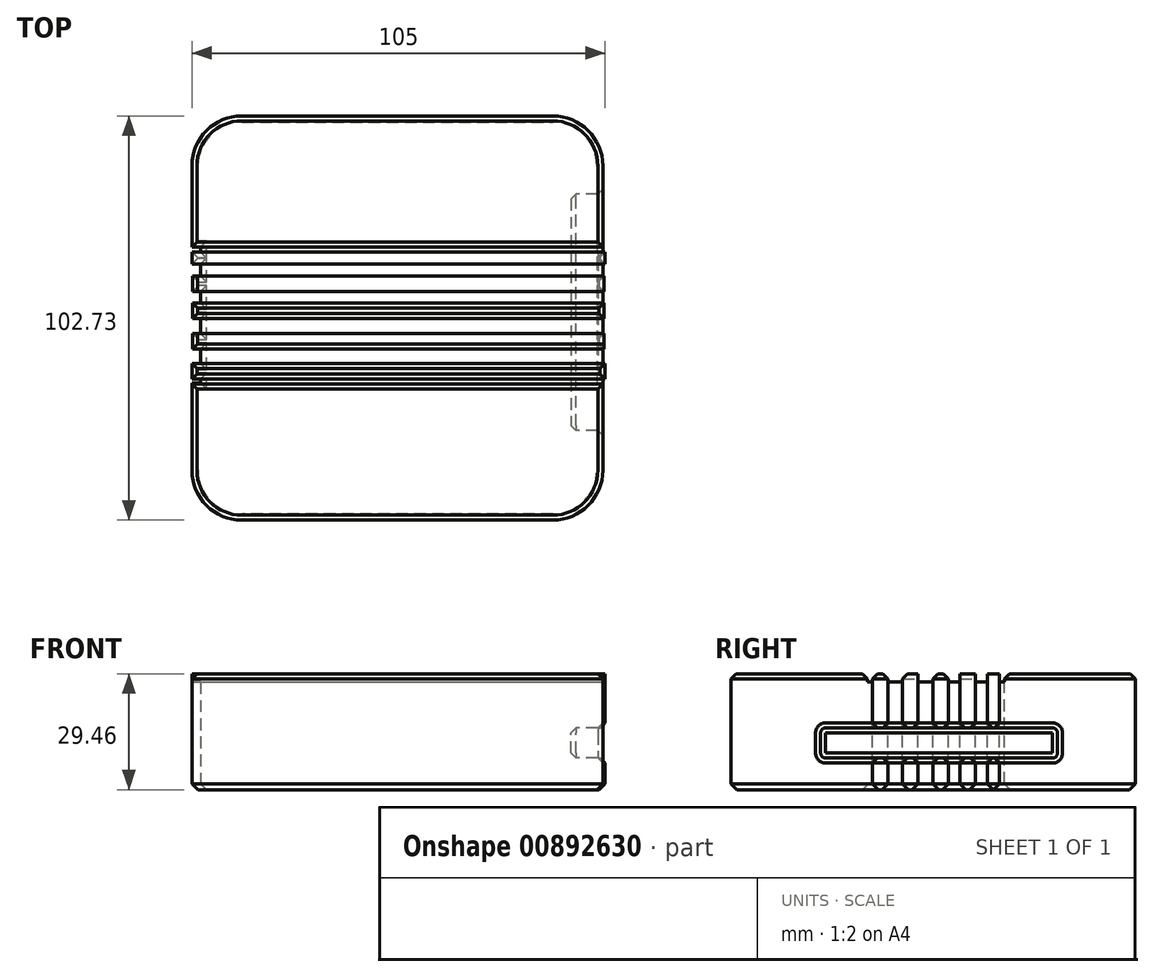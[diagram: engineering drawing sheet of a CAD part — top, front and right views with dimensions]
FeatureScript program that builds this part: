
annotation { "Feature Type Name" : "Feature", "Feature Type Description" : "" }
export const myFeature = defineFeature(function(context is Context, id is Id, definition is map)
    precondition{}
    {
        {
            var Q0;
            Q0=qCreatedBy(makeId("Top.planeOp"),FACE);
            var sketch = newSketch(context, id + "F0", { "sketchPlane" : qUnion([Q0])});
            skLineSegment(sketch, "E0.bottom", {"start": v(-52.2, 52.34) * mm, "end": v(52.2, 52.34) * mm});
            skLineSegment(sketch, "E0.top", {"start": v(-52.2, -50.4) * mm, "end": v(52.2, -50.4) * mm});
            skLineSegment(sketch, "E0.left", {"start": v(-52.2, 52.34) * mm, "end": v(-52.2, -50.4) * mm});
            skLineSegment(sketch, "E0.right", {"start": v(52.2, 52.34) * mm, "end": v(52.2, -50.4) * mm});
            skSolve(sketch);
        }
        {
            var Q0;
            Q0 = qSketchRegion(id + "F0", true);
            extrude(context, id + "F1", {"entities" : qUnion([Q0]), "depth" : 25.4 * mm, "offsetDistance" : 25.4 * mm});
        }
        {
            var Q0;
            Q0=makeQuery(id+"F1.opExtrude","SWEPT_EDGE",EDGE,{"disambiguationData":[OSD([sQuery(id+"F0.wireOp",EDGE,"E0.top"),sQuery(id+"F0.wireOp",EDGE,"E0.left")])]});
            var Q1;
            Q1=makeQuery(id+"F1.opExtrude","SWEPT_EDGE",EDGE,{"disambiguationData":[OSD([sQuery(id+"F0.wireOp",EDGE,"E0.top"),sQuery(id+"F0.wireOp",EDGE,"E0.right")])]});
            var Q2;
            Q2=makeQuery(id+"F1.opExtrude","SWEPT_EDGE",EDGE,{"disambiguationData":[OSD([sQuery(id+"F0.wireOp",EDGE,"E0.bottom"),sQuery(id+"F0.wireOp",EDGE,"E0.left")])]});
            var Q3;
            Q3=makeQuery(id+"F1.opExtrude","SWEPT_EDGE",EDGE,{"disambiguationData":[OSD([sQuery(id+"F0.wireOp",EDGE,"E0.bottom"),sQuery(id+"F0.wireOp",EDGE,"E0.right")])]});
            fillet(context, id + "F2", {"entities" : qUnion([Q0, Q1, Q2, Q3]), "radius" : 12.7 * mm, "tangentPropagation" : true, "allowEdgeOverflow" : false});
        }
        {
            var Q0;
            Q0=makeQuery(id+"F1.opExtrude","CAP_FACE",FACE,{"disambiguationData":[OSD([sQuery(id+"F0.wireOp",EDGE,"E0.bottom"),sQuery(id+"F0.wireOp",EDGE,"E0.top"),sQuery(id+"F0.wireOp",EDGE,"E0.left"),sQuery(id+"F0.wireOp",EDGE,"E0.right")])],"isStart":false});
            var sketch = newSketch(context, id + "F3", { "sketchPlane" : qUnion([Q0])});
            skLineSegment(sketch, "E1.bottom", {"start": v(-52.2, 19.05) * mm, "end": v(52.2, 19.05) * mm});
            skLineSegment(sketch, "E1.top", {"start": v(-52.2, -15.75) * mm, "end": v(52.2, -15.75) * mm});
            skLineSegment(sketch, "E1.left", {"start": v(-52.2, 19.05) * mm, "end": v(-52.2, -15.75) * mm});
            skLineSegment(sketch, "E1.right", {"start": v(52.2, 19.05) * mm, "end": v(52.2, -15.75) * mm});
            skSolve(sketch);
        }
        {
            var Q0;
            Q0=makeQuery(id+"F3.imprint","IMPRINT",FACE,{"disambiguationData":[TD([[makeQuery(id+"F3.imprint","IMPRINT",EDGE,{"derivedFrom":sQuery(id+"F3.wireOp",EDGE,"E1.bottom")}),-1.0]])]});
            extrude(context, id + "F4", {"entities" : qUnion([Q0]), "operationType" : NewBodyOperationType.REMOVE, "oppositeDirection" : true, "depth" : 2.15 * mm, "offsetDistance" : 25.4 * mm});
        }
        {
            var Q0;
            Q0=makeQuery(id+"F1.opExtrude","SWEPT_FACE",FACE,{"disambiguationData":[OSD([sQuery(id+"F0.wireOp",EDGE,"E0.left")])]});
            var sketch = newSketch(context, id + "F5", { "sketchPlane" : qUnion([Q0])});
            skLineSegment(sketch, "E2.bottom", {"start": v(-19.05, 23.25) * mm, "end": v(15.58, 23.25) * mm});
            skLineSegment(sketch, "E2.top", {"start": v(-19.05, 0) * mm, "end": v(15.58, 0) * mm});
            skLineSegment(sketch, "E2.left", {"start": v(-19.05, 23.25) * mm, "end": v(-19.05, 0) * mm});
            skLineSegment(sketch, "E2.right", {"start": v(15.58, 23.25) * mm, "end": v(15.58, 0) * mm});
            skSolve(sketch);
        }
        {
            var Q0;
            Q0=makeQuery(id+"F5.imprint","IMPRINT",FACE,{"disambiguationData":[TD([[makeQuery(id+"F5.imprint","IMPRINT",EDGE,{"derivedFrom":sQuery(id+"F5.wireOp",EDGE,"E2.bottom")}),-1.0]])]});
            extrude(context, id + "F6", {"entities" : qUnion([Q0]), "operationType" : NewBodyOperationType.REMOVE, "oppositeDirection" : true, "depth" : 2.27 * mm, "offsetDistance" : 25.4 * mm});
        }
        {
            var Q0;
            {var subQ0=sQuery(id+"F0.wireOp",EDGE,"E0.left");var subQ1=sQuery(id+"F0.wireOp",EDGE,"E0.bottom");var subQ2=sQuery(id+"F0.wireOp",EDGE,"E0.right");Q0=makeQuery(id+"F4.boolean.opBoolean","SPLIT",FACE,{"disambiguationData":[TD([makeQuery(id+"F1.opExtrude","SWEPT_FACE",FACE,{"disambiguationData":[OSD([subQ1])]})])],"derivedFrom":makeQuery(id+"F1.opExtrude","CAP_FACE",FACE,{"disambiguationData":[OSD([subQ1,sQuery(id+"F0.wireOp",EDGE,"E0.top"),subQ0,subQ2])],"isStart":false})});}
            var sketch = newSketch(context, id + "F7", { "sketchPlane" : qUnion([Q0])});
            skLineSegment(sketch, "E3.bottom", {"start": v(-52.06, 11.67) * mm, "end": v(52.53, 11.67) * mm});
            skLineSegment(sketch, "E3.top", {"start": v(-52.06, 7.72) * mm, "end": v(52.53, 7.72) * mm});
            skLineSegment(sketch, "E3.left", {"start": v(-52.06, 11.67) * mm, "end": v(-52.06, 7.72) * mm});
            skLineSegment(sketch, "E3.right", {"start": v(52.53, 11.67) * mm, "end": v(52.53, 7.72) * mm});
            skLineSegment(sketch, "E4.bottom", {"start": v(-52.03, 4.82) * mm, "end": v(52.56, 4.82) * mm});
            skLineSegment(sketch, "E4.top", {"start": v(-52.03, 0.87) * mm, "end": v(52.56, 0.87) * mm});
            skLineSegment(sketch, "E4.left", {"start": v(-52.03, 4.82) * mm, "end": v(-52.03, 0.87) * mm});
            skLineSegment(sketch, "E4.right", {"start": v(52.56, 4.82) * mm, "end": v(52.56, 0.87) * mm});
            skLineSegment(sketch, "E5.bottom", {"start": v(-52.03, -2.9) * mm, "end": v(52.56, -2.9) * mm});
            skLineSegment(sketch, "E5.top", {"start": v(-52.03, -6.85) * mm, "end": v(52.56, -6.85) * mm});
            skLineSegment(sketch, "E5.left", {"start": v(-52.03, -2.9) * mm, "end": v(-52.03, -6.85) * mm});
            skLineSegment(sketch, "E5.right", {"start": v(52.56, -2.9) * mm, "end": v(52.56, -6.85) * mm});
            skLineSegment(sketch, "E6.bottom", {"start": v(-52.2, -10.52) * mm, "end": v(52.81, -10.52) * mm});
            skLineSegment(sketch, "E6.top", {"start": v(-52.2, -14.47) * mm, "end": v(52.81, -14.47) * mm});
            skLineSegment(sketch, "E6.left", {"start": v(-52.2, -10.52) * mm, "end": v(-52.2, -14.47) * mm});
            skLineSegment(sketch, "E6.right", {"start": v(52.81, -10.52) * mm, "end": v(52.81, -14.47) * mm});
            skLineSegment(sketch, "E7.bottom", {"start": v(-52.2, 14.7) * mm, "end": v(52.77, 14.7) * mm});
            skLineSegment(sketch, "E7.top", {"start": v(-52.2, 17.76) * mm, "end": v(52.77, 17.76) * mm});
            skLineSegment(sketch, "E7.left", {"start": v(-52.2, 14.7) * mm, "end": v(-52.2, 17.76) * mm});
            skLineSegment(sketch, "E7.right", {"start": v(52.77, 14.7) * mm, "end": v(52.77, 17.76) * mm});
            skSolve(sketch);
        }
        {
            var Q0;
            Q0=makeQuery(id+"F7.imprint","IMPRINT",FACE,{"disambiguationData":[TD([[makeQuery(id+"F7.imprint","IMPRINT",EDGE,{"derivedFrom":sQuery(id+"F7.wireOp",EDGE,"E6.bottom")}),-1.0]])]});
            var Q1;
            Q1=makeQuery(id+"F7.imprint","IMPRINT",FACE,{"disambiguationData":[TD([[makeQuery(id+"F7.imprint","IMPRINT",EDGE,{"derivedFrom":sQuery(id+"F7.wireOp",EDGE,"E5.bottom")}),-1.0]])]});
            var Q2;
            Q2=makeQuery(id+"F7.imprint","IMPRINT",FACE,{"disambiguationData":[TD([[makeQuery(id+"F7.imprint","IMPRINT",EDGE,{"derivedFrom":sQuery(id+"F7.wireOp",EDGE,"E4.bottom")}),-1.0]])]});
            var Q3;
            Q3=makeQuery(id+"F7.imprint","IMPRINT",FACE,{"disambiguationData":[TD([[makeQuery(id+"F7.imprint","IMPRINT",EDGE,{"derivedFrom":sQuery(id+"F7.wireOp",EDGE,"E3.bottom")}),-1.0]])]});
            var Q4;
            Q4=makeQuery(id+"F7.imprint","IMPRINT",FACE,{"disambiguationData":[TD([[makeQuery(id+"F7.imprint","IMPRINT",EDGE,{"derivedFrom":sQuery(id+"F7.wireOp",EDGE,"ohG4q9yi-Sl1K-y0JQ-5TuS-v2TCGCpd6eug.top")}),1.0]])]});
            var Q5;
            Q5=makeQuery(id+"F7.imprint","IMPRINT",FACE,{"disambiguationData":[TD([[makeQuery(id+"F7.imprint","IMPRINT",EDGE,{"derivedFrom":sQuery(id+"F7.wireOp",EDGE,"E7.bottom")}),1.0]])]});
            extrude(context, id + "F8", {"entities" : qUnion([Q0, Q1, Q2, Q3, Q4, Q5]), "operationType" : NewBodyOperationType.ADD, "oppositeDirection" : true, "depth" : 25.4 * mm, "offsetDistance" : 25.4 * mm});
        }
        {
            var Q0;
            {var subQ0=sQuery(id+"F0.wireOp",EDGE,"E0.left");Q0=makeQuery(id+"F4.boolean.opBoolean","SPLIT",EDGE,{"disambiguationData":[TD([makeQuery(id+"F4.opExtrude","SWEPT_FACE",FACE,{"disambiguationData":[OSD([sQuery(id+"F3.wireOp",EDGE,"E1.bottom")])]})])],"derivedFrom":makeQuery(id+"F1.opExtrude","CAP_EDGE",EDGE,{"disambiguationData":[OSD([subQ0])],"isStart":false})});}
            var Q1;
            {var subQ0=sQuery(id+"F0.wireOp",EDGE,"E0.left");var subQ1=sQuery(id+"F0.wireOp",EDGE,"E0.bottom");Q1=makeQuery(id+"F2.opFillet","BLEND_EDGE",EDGE,{"blendedFrom":[makeQuery(id+"F1.opExtrude","SWEPT_EDGE",EDGE,{"disambiguationData":[OSD([subQ1,subQ0])]}),makeQuery(id+"F1.opExtrude","CAP_FACE",FACE,{"disambiguationData":[OSD([subQ1,sQuery(id+"F0.wireOp",EDGE,"E0.top"),subQ0,sQuery(id+"F0.wireOp",EDGE,"E0.right")])],"isStart":false})],"blendedInto":[makeQuery(id+"F1.opExtrude","CAP_FACE",FACE,{"disambiguationData":[OSD([subQ1,sQuery(id+"F0.wireOp",EDGE,"E0.top"),subQ0,sQuery(id+"F0.wireOp",EDGE,"E0.right")])],"isStart":false})]});}
            var Q2;
            {var subQ0=sQuery(id+"F0.wireOp",EDGE,"E0.left");var subQ1=sQuery(id+"F0.wireOp",EDGE,"E0.bottom");var subQ2=sQuery(id+"F0.wireOp",EDGE,"E0.right");Q2=makeQuery(id+"F4.boolean.opBoolean","SPLIT",FACE,{"disambiguationData":[TD([makeQuery(id+"F1.opExtrude","SWEPT_FACE",FACE,{"disambiguationData":[OSD([subQ1])]})])],"derivedFrom":makeQuery(id+"F1.opExtrude","CAP_FACE",FACE,{"disambiguationData":[OSD([subQ1,sQuery(id+"F0.wireOp",EDGE,"E0.top"),subQ0,subQ2])],"isStart":false})});}
            var Q3;
            Q3=makeQuery(id+"F8.opExtrude","CAP_FACE",FACE,{"disambiguationData":[OSD([sQuery(id+"F7.wireOp",EDGE,"E6.bottom"),sQuery(id+"F7.wireOp",EDGE,"E6.top"),sQuery(id+"F7.wireOp",EDGE,"E6.left"),sQuery(id+"F7.wireOp",EDGE,"E6.right")])],"isStart":true});
            var Q4;
            Q4=makeQuery(id+"F8.opExtrude","CAP_EDGE",EDGE,{"disambiguationData":[OSD([sQuery(id+"F7.wireOp",EDGE,"E5.top")])],"isStart":true});
            var Q5;
            Q5=makeQuery(id+"F8.opExtrude","CAP_FACE",FACE,{"disambiguationData":[OSD([sQuery(id+"F7.wireOp",EDGE,"E4.bottom"),sQuery(id+"F7.wireOp",EDGE,"E4.top"),sQuery(id+"F7.wireOp",EDGE,"E4.left"),sQuery(id+"F7.wireOp",EDGE,"E4.right")])],"isStart":true});
            var Q6;
            Q6=makeQuery(id+"F8.opExtrude","CAP_EDGE",EDGE,{"disambiguationData":[OSD([sQuery(id+"F7.wireOp",EDGE,"E3.left")])],"isStart":true});
            var Q7;
            Q7=makeQuery(id+"F8.opExtrude","CAP_EDGE",EDGE,{"disambiguationData":[OSD([sQuery(id+"F7.wireOp",EDGE,"E4.left")])],"isStart":true});
            var Q8;
            Q8=makeQuery(id+"F8.opExtrude","CAP_EDGE",EDGE,{"disambiguationData":[OSD([sQuery(id+"F7.wireOp",EDGE,"E5.left")])],"isStart":true});
            var Q9;
            {var subQ0=sQuery(id+"F0.wireOp",EDGE,"E0.right");var subQ1=sQuery(id+"F0.wireOp",EDGE,"E0.left");var subQ2=sQuery(id+"F0.wireOp",EDGE,"E0.top");Q9=makeQuery(id+"F4.boolean.opBoolean","SPLIT",FACE,{"disambiguationData":[TD([makeQuery(id+"F1.opExtrude","SWEPT_FACE",FACE,{"disambiguationData":[OSD([subQ2])]})])],"derivedFrom":makeQuery(id+"F1.opExtrude","CAP_FACE",FACE,{"disambiguationData":[OSD([sQuery(id+"F0.wireOp",EDGE,"E0.bottom"),subQ2,subQ1,subQ0])],"isStart":false})});}
            chamfer(context, id + "F9", {"entities" : qUnion([Q0, Q1, Q2, Q3, Q4, Q5, Q6, Q7, Q8, Q9]), "width" : 1.27 * mm, "tangentPropagation" : true});
        }
        {
            var Q0;
            {var subQ1=sQuery(id+"F3.wireOp",EDGE,"E1.top");var subQ2=sQuery(id+"F0.wireOp",EDGE,"E0.right");Q0=makeQuery(id+"F8.boolean.opBoolean","SPLIT",FACE,{"disambiguationData":[TD([makeQuery(id+"F4.boolean.opBoolean","COPY",FACE,{"derivedFrom":makeQuery(id+"F4.opExtrude","SWEPT_FACE",FACE,{"disambiguationData":[OSD([subQ1])]})})])],"derivedFrom":makeQuery(id+"F1.opExtrude","SWEPT_FACE",FACE,{"disambiguationData":[OSD([subQ2])]})});}
            var sketch = newSketch(context, id + "F10", { "sketchPlane" : qUnion([Q0])});
            skPoint(sketch, "E8.firstSnap0", {"position": v(-14.47, 11.62) * mm});
            skLineSegment(sketch, "E8.bottom", {"start": v(-26.38, 11.62) * mm, "end": v(31.25, 11.62) * mm});
            skLineSegment(sketch, "E8.top", {"start": v(-26.38, 3.94) * mm, "end": v(31.25, 3.94) * mm});
            skLineSegment(sketch, "E8.left", {"start": v(-27.65, 10.35) * mm, "end": v(-27.65, 5.21) * mm});
            skLineSegment(sketch, "E8.right", {"start": v(32.52, 10.35) * mm, "end": v(32.52, 5.21) * mm});
            skPoint(sketch, "E9.visualSharp", {"position": v(-27.65, 11.62) * mm});
            skArc(sketch, "E9.filletArc", {"start": v(-26.38, 11.62) * mm, "mid": v(-27.28, 11.25) * mm, "end": v(-27.65, 10.35) * mm});
            skPoint(sketch, "E10.visualSharp", {"position": v(-27.65, 3.94) * mm});
            skArc(sketch, "E10.filletArc", {"start": v(-27.65, 5.21) * mm, "mid": v(-27.28, 4.32) * mm, "end": v(-26.38, 3.94) * mm});
            skPoint(sketch, "E11.visualSharp", {"position": v(32.52, 3.94) * mm});
            skArc(sketch, "E11.filletArc", {"start": v(31.25, 3.94) * mm, "mid": v(32.15, 4.32) * mm, "end": v(32.52, 5.21) * mm});
            skPoint(sketch, "E12.visualSharp", {"position": v(32.52, 11.62) * mm});
            skArc(sketch, "E12.filletArc", {"start": v(32.52, 10.35) * mm, "mid": v(32.15, 11.25) * mm, "end": v(31.25, 11.62) * mm});
            skSolve(sketch);
        }
        {
            var Q0;
            Q0 = qSketchRegion(id + "F10", true);
            extrude(context, id + "F11", {"entities" : qUnion([Q0]), "operationType" : NewBodyOperationType.REMOVE, "depth" : 18.54 * mm, "offsetDistance" : 25.4 * mm, "hasSecondDirection" : true, "secondDirectionOppositeDirection" : true, "secondDirectionDepth" : 8.13 * mm});
        }
        {
            var Q0;
            {var subQ1=sQuery(id+"F3.wireOp",EDGE,"E1.top");var subQ2=sQuery(id+"F0.wireOp",EDGE,"E0.right");Q0=makeQuery(id+"F11.boolean.opBoolean","INTERSECT",EDGE,{"derivedFrom":[makeQuery(id+"F8.boolean.opBoolean","SPLIT",FACE,{"disambiguationData":[TD([makeQuery(id+"F4.boolean.opBoolean","COPY",FACE,{"derivedFrom":makeQuery(id+"F4.opExtrude","SWEPT_FACE",FACE,{"disambiguationData":[OSD([subQ1])]})})])],"derivedFrom":makeQuery(id+"F1.opExtrude","SWEPT_FACE",FACE,{"disambiguationData":[OSD([subQ2])]})}),makeQuery(id+"F11.opExtrude","SWEPT_FACE",FACE,{"disambiguationData":[OSD([sQuery(id+"F10.wireOp",EDGE,"E8.bottom")])]})]});}
            var Q1;
            {var subQ1=sQuery(id+"F3.wireOp",EDGE,"E1.bottom");var subQ2=sQuery(id+"F0.wireOp",EDGE,"E0.right");Q1=makeQuery(id+"F11.boolean.opBoolean","INTERSECT",EDGE,{"derivedFrom":[makeQuery(id+"F8.boolean.opBoolean","SPLIT",FACE,{"disambiguationData":[TD([makeQuery(id+"F4.boolean.opBoolean","COPY",FACE,{"derivedFrom":makeQuery(id+"F4.opExtrude","SWEPT_FACE",FACE,{"disambiguationData":[OSD([subQ1])]})})])],"derivedFrom":makeQuery(id+"F1.opExtrude","SWEPT_FACE",FACE,{"disambiguationData":[OSD([subQ2])]})}),makeQuery(id+"F11.opExtrude","SWEPT_FACE",FACE,{"disambiguationData":[OSD([sQuery(id+"F10.wireOp",EDGE,"E8.bottom")])]})]});}
            var Q2;
            Q2=makeQuery(id+"F11.boolean.opBoolean","INTERSECT",EDGE,{"derivedFrom":[makeQuery(id+"F8.opExtrude","SWEPT_FACE",FACE,{"disambiguationData":[OSD([sQuery(id+"F7.wireOp",EDGE,"E7.right")])]}),makeQuery(id+"F11.opExtrude","SWEPT_FACE",FACE,{"disambiguationData":[OSD([sQuery(id+"F10.wireOp",EDGE,"E8.top")])]})]});
            var Q3;
            Q3=makeQuery(id+"F11.boolean.opBoolean","COPY",FACE,{"derivedFrom":makeQuery(id+"F11.opExtrude","SWEPT_FACE",FACE,{"disambiguationData":[OSD([sQuery(id+"F10.wireOp",EDGE,"E8.top")])]})});
            var Q4;
            Q4=makeQuery(id+"F11.boolean.opBoolean","COPY",FACE,{"derivedFrom":makeQuery(id+"F11.opExtrude","SWEPT_FACE",FACE,{"disambiguationData":[OSD([sQuery(id+"F10.wireOp",EDGE,"E8.bottom")])]})});
            chamfer(context, id + "F12", {"entities" : qUnion([Q0, Q1, Q2, Q3, Q4]), "width" : 1.27 * mm, "tangentPropagation" : true});
        }
        {
            var Q0;
            Q0=makeQuery(id+"F8.boolean.opBoolean","MERGE",FACE,{"derivedFrom":[makeQuery(id+"F1.opExtrude","CAP_FACE",FACE,{"disambiguationData":[OSD([sQuery(id+"F0.wireOp",EDGE,"E0.bottom"),sQuery(id+"F0.wireOp",EDGE,"E0.top"),sQuery(id+"F0.wireOp",EDGE,"E0.left"),sQuery(id+"F0.wireOp",EDGE,"E0.right")])],"isStart":true}),makeQuery(id+"F8.opExtrude","CAP_FACE",FACE,{"disambiguationData":[OSD([sQuery(id+"F7.wireOp",EDGE,"E3.bottom"),sQuery(id+"F7.wireOp",EDGE,"E3.top"),sQuery(id+"F7.wireOp",EDGE,"E3.left"),sQuery(id+"F7.wireOp",EDGE,"E3.right")])],"isStart":false}),makeQuery(id+"F8.opExtrude","CAP_FACE",FACE,{"disambiguationData":[OSD([sQuery(id+"F7.wireOp",EDGE,"E4.bottom"),sQuery(id+"F7.wireOp",EDGE,"E4.top"),sQuery(id+"F7.wireOp",EDGE,"E4.left"),sQuery(id+"F7.wireOp",EDGE,"E4.right")])],"isStart":false}),makeQuery(id+"F8.opExtrude","CAP_FACE",FACE,{"disambiguationData":[OSD([sQuery(id+"F7.wireOp",EDGE,"E5.bottom"),sQuery(id+"F7.wireOp",EDGE,"E5.top"),sQuery(id+"F7.wireOp",EDGE,"E5.left"),sQuery(id+"F7.wireOp",EDGE,"E5.right")])],"isStart":false}),makeQuery(id+"F8.opExtrude","CAP_FACE",FACE,{"disambiguationData":[OSD([sQuery(id+"F7.wireOp",EDGE,"E6.bottom"),sQuery(id+"F7.wireOp",EDGE,"E6.top"),sQuery(id+"F7.wireOp",EDGE,"E6.left"),sQuery(id+"F7.wireOp",EDGE,"E6.right")])],"isStart":false}),makeQuery(id+"F8.opExtrude","CAP_FACE",FACE,{"disambiguationData":[OSD([sQuery(id+"F7.wireOp",EDGE,"E7.bottom"),sQuery(id+"F7.wireOp",EDGE,"E7.top"),sQuery(id+"F7.wireOp",EDGE,"E7.left"),sQuery(id+"F7.wireOp",EDGE,"E7.right")])],"isStart":false})]});
            extrude(context, id + "F13", {"entities" : qUnion([Q0]), "operationType" : NewBodyOperationType.ADD, "depth" : 4.06 * mm, "offsetDistance" : 25.4 * mm});
        }
        {
            var Q0;
            Q0=makeQuery(id+"F13.opExtrude","CAP_FACE",FACE,{"disambiguationData":[OSD([sQuery(id+"F0.wireOp",EDGE,"E0.bottom"),sQuery(id+"F0.wireOp",EDGE,"E0.top"),sQuery(id+"F0.wireOp",EDGE,"E0.left"),sQuery(id+"F0.wireOp",EDGE,"E0.right"),sQuery(id+"F7.wireOp",EDGE,"E3.bottom"),sQuery(id+"F7.wireOp",EDGE,"E3.top"),sQuery(id+"F7.wireOp",EDGE,"E3.left"),sQuery(id+"F7.wireOp",EDGE,"E3.right"),sQuery(id+"F7.wireOp",EDGE,"E4.bottom"),sQuery(id+"F7.wireOp",EDGE,"E4.top"),sQuery(id+"F7.wireOp",EDGE,"E4.left"),sQuery(id+"F7.wireOp",EDGE,"E4.right"),sQuery(id+"F7.wireOp",EDGE,"E5.bottom"),sQuery(id+"F7.wireOp",EDGE,"E5.top"),sQuery(id+"F7.wireOp",EDGE,"E5.left"),sQuery(id+"F7.wireOp",EDGE,"E5.right"),sQuery(id+"F7.wireOp",EDGE,"E6.bottom"),sQuery(id+"F7.wireOp",EDGE,"E6.top"),sQuery(id+"F7.wireOp",EDGE,"E6.left"),sQuery(id+"F7.wireOp",EDGE,"E6.right"),sQuery(id+"F7.wireOp",EDGE,"E7.bottom"),sQuery(id+"F7.wireOp",EDGE,"E7.top"),sQuery(id+"F7.wireOp",EDGE,"E7.left"),sQuery(id+"F7.wireOp",EDGE,"E7.right")])],"isStart":false});
            chamfer(context, id + "F14", {"entities" : qUnion([Q0]), "width" : 1.52 * mm, "tangentPropagation" : true});
        }
    });
